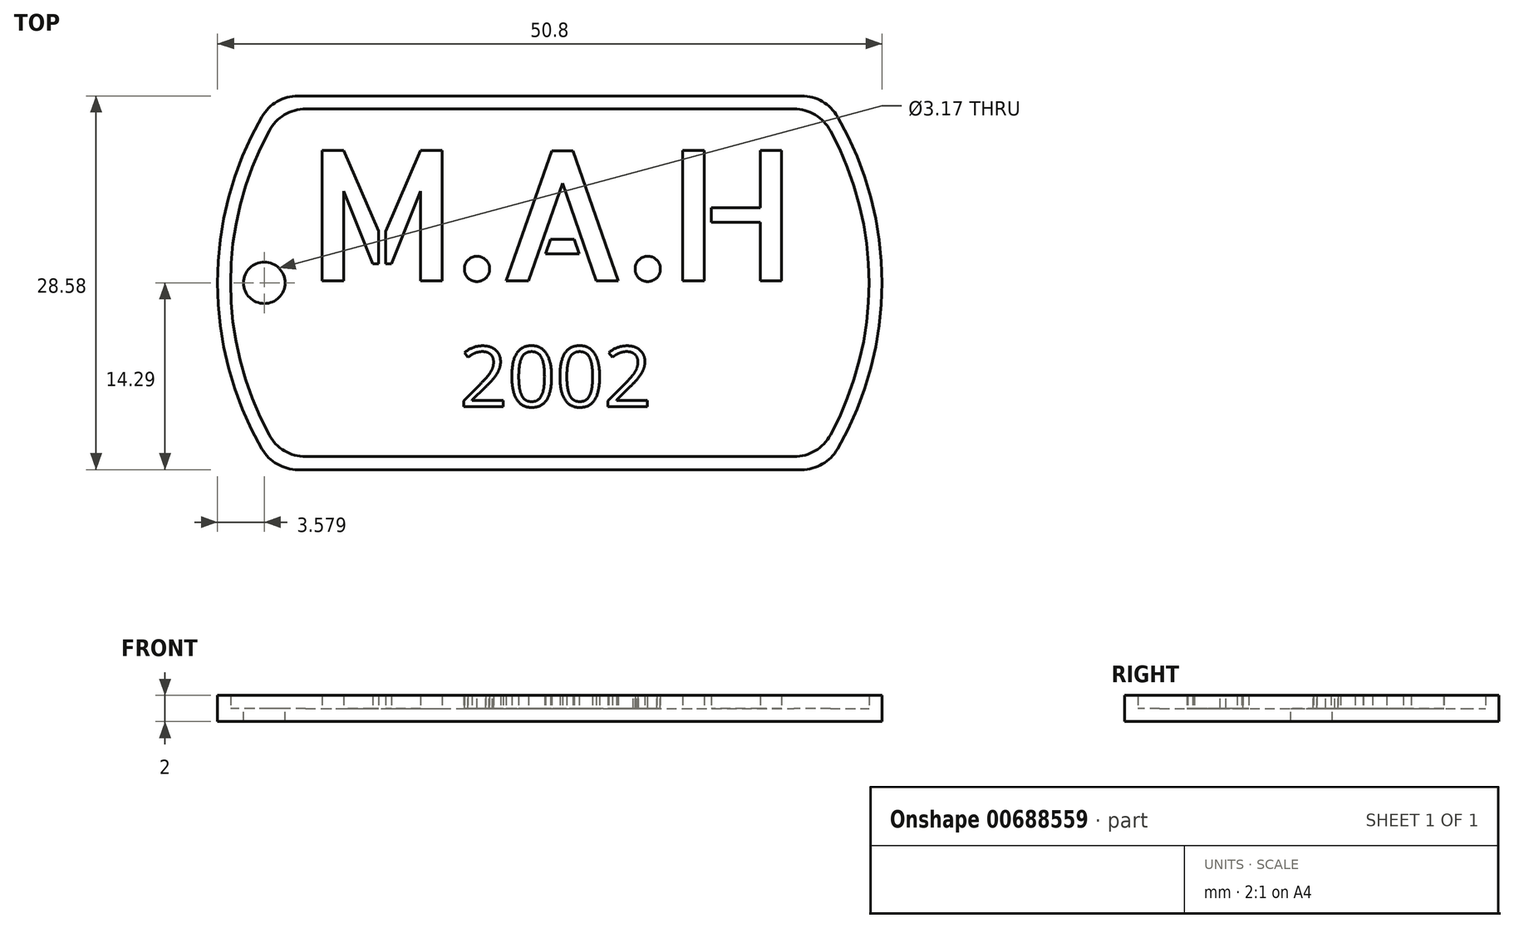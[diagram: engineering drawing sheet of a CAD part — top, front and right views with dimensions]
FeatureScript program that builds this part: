
annotation { "Feature Type Name" : "Feature", "Feature Type Description" : "" }
export const myFeature = defineFeature(function(context is Context, id is Id, definition is map)
    precondition{}
    {
        {
            var Q0;
            Q0=qCreatedBy(makeId("Top.planeOp"),FACE);
            var sketch = newSketch(context, id + "F0", { "sketchPlane" : qUnion([Q0])});
            skArc(sketch, "E0", {"start": v(-22, 12.7) * mm, "mid": v(-25.4, 0) * mm, "end": v(-22, -12.7) * mm});
            skLineSegment(sketch, "E1.top", {"start": v(-19.25, -14.29) * mm, "end": v(19.25, -14.29) * mm});
            skArc(sketch, "E2.trimOffspring", {"start": v(22, -12.7) * mm, "mid": v(25.4, 0) * mm, "end": v(22, 12.7) * mm});
            skLineSegment(sketch, "E3", {"start": v(-19.25, 14.29) * mm, "end": v(19.25, 14.29) * mm});
            skPoint(sketch, "E4.visualSharp", {"position": v(-21, 14.29) * mm});
            skArc(sketch, "E4.filletArc", {"start": v(-19.25, 14.29) * mm, "mid": v(-20.83, 13.86) * mm, "end": v(-22, 12.7) * mm});
            skPoint(sketch, "E5.visualSharp", {"position": v(21, 14.29) * mm});
            skArc(sketch, "E5.filletArc", {"start": v(22, 12.7) * mm, "mid": v(20.83, 13.86) * mm, "end": v(19.25, 14.29) * mm});
            skPoint(sketch, "E6.visualSharp", {"position": v(21, -14.29) * mm});
            skArc(sketch, "E6.filletArc", {"start": v(19.25, -14.29) * mm, "mid": v(20.83, -13.86) * mm, "end": v(22, -12.7) * mm});
            skPoint(sketch, "E7.visualSharp", {"position": v(-21, -14.29) * mm});
            skArc(sketch, "E7.filletArc", {"start": v(-22, -12.7) * mm, "mid": v(-20.83, -13.86) * mm, "end": v(-19.25, -14.29) * mm});
            skSolve(sketch);
        }
        {
            var Q0;
            Q0=makeQuery(id+"F0.imprint","IMPRINT",FACE,{"disambiguationData":[TD([[makeQuery(id+"F0.imprint","IMPRINT",EDGE,{"derivedFrom":sQuery(id+"F0.wireOp",EDGE,"E0")}),1.0]])]});
            extrude(context, id + "F1", {"entities" : qUnion([Q0]), "depth" : 1 * mm, "offsetDistance" : 25.4 * mm});
        }
        {
            var Q0;
            Q0=makeQuery(id+"F1.opExtrude","CAP_FACE",FACE,{"disambiguationData":[OSD([sQuery(id+"F0.wireOp",EDGE,"E0"),sQuery(id+"F0.wireOp",EDGE,"E1.top"),sQuery(id+"F0.wireOp",EDGE,"E2.trimOffspring"),sQuery(id+"F0.wireOp",EDGE,"E3"),sQuery(id+"F0.wireOp",EDGE,"E4.filletArc"),sQuery(id+"F0.wireOp",EDGE,"E5.filletArc"),sQuery(id+"F0.wireOp",EDGE,"E6.filletArc"),sQuery(id+"F0.wireOp",EDGE,"E7.filletArc")])],"isStart":false});
            var sketch = newSketch(context, id + "F2", { "sketchPlane" : qUnion([Q0])});
            skLineSegment(sketch, "E8.0", {"start": v(-18.66, 13.29) * mm, "end": v(18.66, 13.29) * mm});
            skArc(sketch, "E8.1", {"start": v(-21.45, 11.63) * mm, "mid": v(-24.4, 0) * mm, "end": v(-21.45, -11.63) * mm});
            skLineSegment(sketch, "E8.2", {"start": v(-18.66, -13.29) * mm, "end": v(18.66, -13.29) * mm});
            skArc(sketch, "E8.3", {"start": v(21.45, -11.63) * mm, "mid": v(24.4, 0) * mm, "end": v(21.45, 11.63) * mm});
            skPoint(sketch, "E9.visualSharp", {"position": v(-20.46, 13.29) * mm});
            skArc(sketch, "E9.filletArc", {"start": v(-18.66, 13.29) * mm, "mid": v(-20.29, 12.84) * mm, "end": v(-21.45, 11.63) * mm});
            skPoint(sketch, "E10.visualSharp", {"position": v(20.46, 13.29) * mm});
            skArc(sketch, "E10.filletArc", {"start": v(21.45, 11.63) * mm, "mid": v(20.29, 12.84) * mm, "end": v(18.66, 13.29) * mm});
            skPoint(sketch, "E11.visualSharp", {"position": v(20.46, -13.29) * mm});
            skArc(sketch, "E11.filletArc", {"start": v(18.66, -13.29) * mm, "mid": v(20.29, -12.84) * mm, "end": v(21.45, -11.63) * mm});
            skPoint(sketch, "E12.visualSharp", {"position": v(-20.46, -13.29) * mm});
            skArc(sketch, "E12.filletArc", {"start": v(-21.45, -11.63) * mm, "mid": v(-20.29, -12.84) * mm, "end": v(-18.66, -13.29) * mm});
            skLineSegment(sketch, "E13.0", {"start": v(-19.25, 14.29) * mm, "end": v(19.25, 14.29) * mm});
            skArc(sketch, "E13.1", {"start": v(-22, 12.7) * mm, "mid": v(-25.4, 0) * mm, "end": v(-22, -12.7) * mm});
            skLineSegment(sketch, "E13.2", {"start": v(-19.25, -14.29) * mm, "end": v(19.25, -14.29) * mm});
            skArc(sketch, "E13.3", {"start": v(22, -12.7) * mm, "mid": v(25.4, 0) * mm, "end": v(22, 12.7) * mm});
            skPoint(sketch, "E14.visualSharp", {"position": v(-21, -14.29) * mm});
            skArc(sketch, "E14.filletArc", {"start": v(-22, -12.7) * mm, "mid": v(-20.83, -13.86) * mm, "end": v(-19.25, -14.29) * mm});
            skPoint(sketch, "E15.visualSharp", {"position": v(21, -14.29) * mm});
            skArc(sketch, "E15.filletArc", {"start": v(19.25, -14.29) * mm, "mid": v(20.83, -13.86) * mm, "end": v(22, -12.7) * mm});
            skPoint(sketch, "E16.visualSharp", {"position": v(21, 14.29) * mm});
            skArc(sketch, "E16.filletArc", {"start": v(22, 12.7) * mm, "mid": v(20.83, 13.86) * mm, "end": v(19.25, 14.29) * mm});
            skPoint(sketch, "E17.visualSharp", {"position": v(-21, 14.29) * mm});
            skArc(sketch, "E17.filletArc", {"start": v(-19.25, 14.29) * mm, "mid": v(-20.83, 13.86) * mm, "end": v(-22, 12.7) * mm});
            skSolve(sketch);
        }
        {
            var Q0;
            Q0=makeQuery(id+"F2.imprint","IMPRINT",FACE,{"disambiguationData":[TD([[makeQuery(id+"F2.imprint","IMPRINT",EDGE,{"derivedFrom":sQuery(id+"F2.wireOp",EDGE,"E8.0")}),1.0]])]});
            extrude(context, id + "F3", {"entities" : qUnion([Q0]), "operationType" : NewBodyOperationType.ADD, "depth" : 1 * mm, "offsetDistance" : 25.4 * mm});
        }
        {
            var Q0;
            Q0=makeQuery(id+"F1.opExtrude","CAP_FACE",FACE,{"disambiguationData":[OSD([sQuery(id+"F0.wireOp",EDGE,"E0"),sQuery(id+"F0.wireOp",EDGE,"E1.top"),sQuery(id+"F0.wireOp",EDGE,"E2.trimOffspring"),sQuery(id+"F0.wireOp",EDGE,"E3"),sQuery(id+"F0.wireOp",EDGE,"E4.filletArc"),sQuery(id+"F0.wireOp",EDGE,"E5.filletArc"),sQuery(id+"F0.wireOp",EDGE,"E6.filletArc"),sQuery(id+"F0.wireOp",EDGE,"E7.filletArc")])],"isStart":false});
            var sketch = newSketch(context, id + "F4", { "sketchPlane" : qUnion([Q0])});
            skCircle(sketch, "E18", {"center": v(-21.82, 0) * mm, "radius": 1.59 * mm});
            skSolve(sketch);
        }
        {
            var Q0;
            Q0=makeQuery(id+"F4.imprint","IMPRINT",FACE,{"disambiguationData":[TD([[makeQuery(id+"F4.imprint","IMPRINT",EDGE,{"derivedFrom":sQuery(id+"F4.wireOp",EDGE,"E18")}),1.0]])]});
            extrude(context, id + "F5", {"entities" : qUnion([Q0]), "operationType" : NewBodyOperationType.REMOVE, "oppositeDirection" : true, "depth" : 1 * mm, "offsetDistance" : 25.4 * mm});
        }
        {
            var Q0;
            Q0=makeQuery(id+"F1.opExtrude","CAP_FACE",FACE,{"disambiguationData":[OSD([sQuery(id+"F0.wireOp",EDGE,"E0"),sQuery(id+"F0.wireOp",EDGE,"E1.top"),sQuery(id+"F0.wireOp",EDGE,"E2.trimOffspring"),sQuery(id+"F0.wireOp",EDGE,"E3"),sQuery(id+"F0.wireOp",EDGE,"E4.filletArc"),sQuery(id+"F0.wireOp",EDGE,"E5.filletArc"),sQuery(id+"F0.wireOp",EDGE,"E6.filletArc"),sQuery(id+"F0.wireOp",EDGE,"E7.filletArc")])],"isStart":false});
            var sketch = newSketch(context, id + "F6", { "sketchPlane" : qUnion([Q0])});
            skText(sketch, "E19", { "text": "M.A.H", "fontName": "AllertaStencil-Regular.ttf"});
            skText(sketch, "E20", { "text": "2002", "fontName": "OpenSans-Regular.ttf"});
            const initialGuessF6  = {"E19": [-0.01866, 0.00015, 1, 0, 0.00996], "E20": [-0.0069, -0.00947, 1, 0, 0.00463]};
            skSetInitialGuess(sketch, initialGuessF6);
            skSolve(sketch);
        }
        {
            var Q0;
            Q0 = qSketchRegion(id + "F6", true);
            extrude(context, id + "F7", {"entities" : qUnion([Q0]), "operationType" : NewBodyOperationType.ADD, "depth" : 1 * mm, "offsetDistance" : 25.4 * mm});
        }
    });
